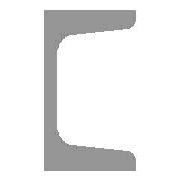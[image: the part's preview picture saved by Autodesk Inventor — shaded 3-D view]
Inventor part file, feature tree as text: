
AUTODESK INVENTOR PART (.ipt)
format: ipt  version: 2025.1 (Build 291241020, 241B)  size: 141,824 bytes
history: native  units: mm (DEFAULTED — no unit token found)
features: other x4, sketch x1, plane x1
ambient origin geometry x8: Origin, YZ Plane, XZ Plane, XY Plane, X Axis, Y Axis, Z Axis, Center Point
bodies: Solid1 (feature_tree), Body (feature_tree)
feature tree (6):
  parser-record x1  (decoder bookkeeping rows leaked as tree rows — omitted from the tree; the rows remain in map.json)
  other  "Driven Length"
  other  "Start Plane"
  other  "End Plane"
  sketch  "Sketch3"  dims[d0=5.9mm d1=50.0mm d2=50.0mm d3=8.0mm d4=22.05mm d5=2.317543mm d6=2400.0mm d7=0.0mm d23=8.0mm d24=4.5mm d25=1.51mm d26=-0.0mm d27=2400.0mm d28=90.0deg d29=2400.0mm]
  plane  "Work Plane3"
